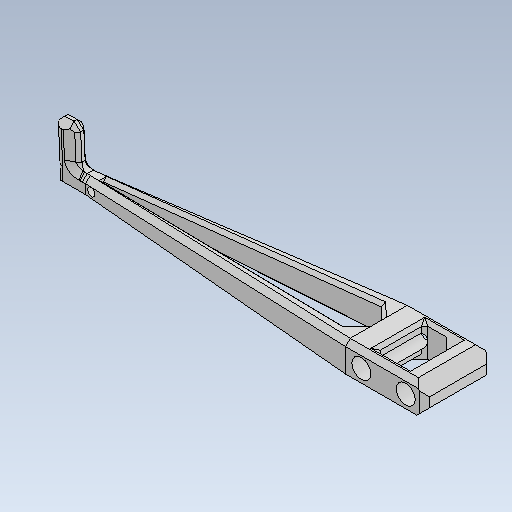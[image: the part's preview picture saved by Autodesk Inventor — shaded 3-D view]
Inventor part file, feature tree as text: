
AUTODESK INVENTOR PART (.ipt)
format: ipt  version: 2023 (Build 270158030, 158C)  size: 285,184 bytes
history: native  units: mm
features: other x4, extrude x1, chamfer x1, sketch x1
ambient origin geometry x8: Origin, YZ Plane, XZ Plane, XY Plane, X Axis, Y Axis, Z Axis, Center Point
bodies: Body1 (feature_tree)
feature tree (7):
  other  "trebuchet-complete-parts.ipt"
  extrude  "Extrusion1"  Depth=3.0mm
  chamfer  "Chamfer1"  Distance=8.0mm
  other  "throw-arm-top::trebuchet-complete-parts.ipt"
  other  "TaggingFeature1"
  sketch  "Sketch1"  dims[d0=10.0mm d1=3.0mm d2=8.0mm d3=2.0mm d4=0.0mm d5=1.5mm d6=2.0mm d7=45.0deg]
  other  "throw-arm-top"
